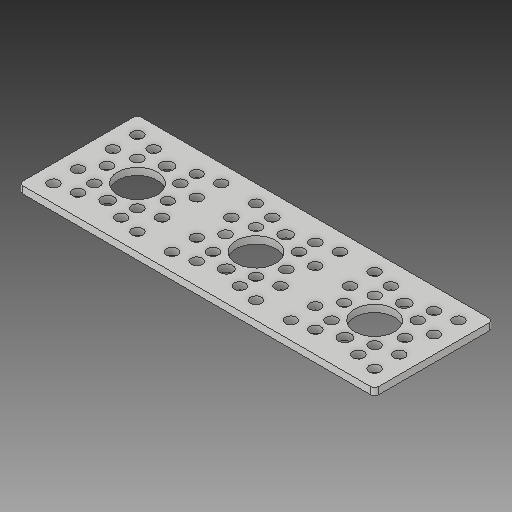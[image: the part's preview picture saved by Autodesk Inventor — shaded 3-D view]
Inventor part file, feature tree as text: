
AUTODESK INVENTOR PART (.ipt)
format: ipt  version: 2019 (Build 230136000, 136)  size: 202,240 bytes
history: native  units: in
note: dims shown in document units (in); Inventor stores cm internally (conversion verified against a paired STEP export)
features: fillet x1
ambient origin geometry x8: Origin, YZ Plane, XZ Plane, XY Plane, X Axis, Y Axis, Z Axis, Center Point
bodies: Solid1 (feature_tree)
feature tree (1):
  fillet  "Fillet1"  [1 undecoded]
note: 1 required parameter value undecoded (feature->parameter linkage not recoverable at this tier; creation-order binding heuristic only, values carry confidence <= 0.55)
